# Revit family: Sanitary_Toilet-Seats_DURAVIT-AG_Starck-1-Toilet-seat-419x453x42-mm-006581
name_source: partatom
category: Specialty Equipment
revit_build: Autodesk Revit 2018 (Build: 20180329_1100(x64)
units: mm (PartAtom-declared; Revit-internal decimal feet)

## family parameters
Always vertical = No
Cut with Voids When Loaded = No
OmniClass Number = 23.31.19.19.17
OmniClass Title = Water Closet Seats
Part Type = Normal
Room Calculation Point = No
Round Connector Dimension = Use Diameter
Shared = No
Work Plane-Based = Yes

## types (1)
- Starck 1 Toilet seat 419x453x42 mm - 006581
    BIMobject category = Toilet Seats
    Default Elevation = 1219.2 mm  [stored 4 ft]
    Description = Duravit Starck 1 Toilet seat White 419x453x42 mm - 0065810000
    Design country = Germany
    ETIM classification = EC011196 | Toilet seat
    Edition number = 1
    IFC Classification = Furnishing Element
    Installation instructions = https://duravit-public-assets.s3.eu-central-1.amazonaws.com
    Main material = Duravit - Plastic - 00 - White Alpin
    Manufacturer = Duravit
    Manufacturer name = DURAVIT AG
    Masterformat 2014 Code = 22 41 13.13
    Masterformat 2014 Description = Residential Water Closets
    Material main = Duroplast
    Model = Starck 1 Toilet seat 419x453x42 mm - 006581
    OmniClass Code = 23-31 19 19 17
    OmniClass Description = Water Closet Seats
    Product Guid = 01a0c8a6-ab88-406d-a348-9350a08fe8a5
    Product SKU = Starck-1-Toilet-seat-419x453x42-mm-006581
    Product certification = http://pro.duravit.com
    Product data url = https://bimobject.com
    Product family = Starck 1
    Product group = Toilet seat
    Product name = Starck 1 Toilet seat 419x453x42 mm - 006581
    Product url = http://pro.duravit.com
    QR code = https://bimobject.com
    Technical description = http://pro.duravit.com
    UNSPSC Code = 301815
    URL = https://www.duravit.com
    Uniclass 2015 Code = Pr_40_20_93_95
    Uniclass 2015 Name = WC seats and covers
    Uniformat II Code = E2010
    Uniformat II Description = Fixed Furnishings
    Youtube clip = http://pro.duravit.com

note: [stored X ft] marks values corroborated as IEEE doubles in the binary element streams (Revit-internal decimal feet)

## geometry (parser evidence)
native form markers: Sweep x4
no freeform markers — native parametric forms only
